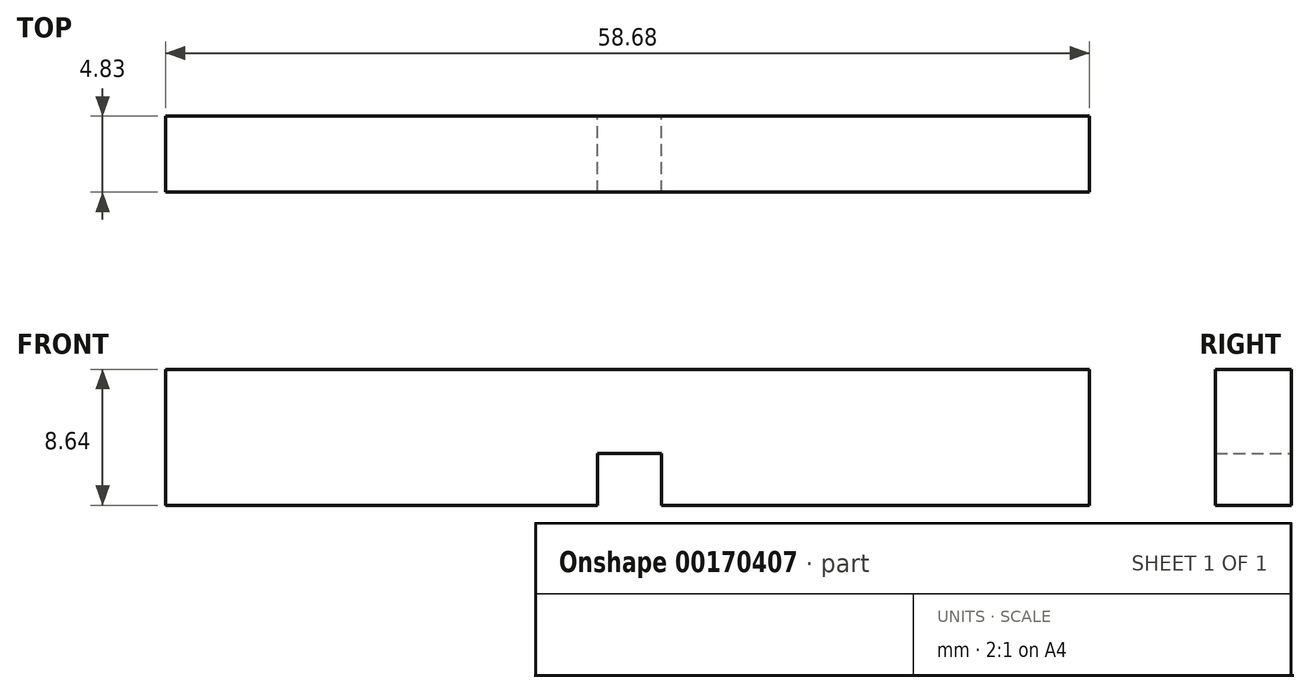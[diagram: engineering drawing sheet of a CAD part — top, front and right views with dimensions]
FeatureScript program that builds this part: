
annotation { "Feature Type Name" : "Feature", "Feature Type Description" : "" }
export const myFeature = defineFeature(function(context is Context, id is Id, definition is map)
    precondition{}
    {
        {
            var Q0;
            Q0=qCreatedBy(makeId("Front.planeOp"),FACE);
            var sketch = newSketch(context, id + "F0", { "sketchPlane" : qUnion([Q0])});
            skLineSegment(sketch, "E0.bottom", {"start": v(-29.34, 4.32) * mm, "end": v(29.34, 4.32) * mm});
            skLineSegment(sketch, "E0.top", {"start": v(-29.34, -4.32) * mm, "end": v(-1.9, -4.32) * mm});
            skLineSegment(sketch, "E0.left", {"start": v(-29.34, 4.32) * mm, "end": v(-29.34, -4.32) * mm});
            skLineSegment(sketch, "E0.right", {"start": v(29.34, 4.32) * mm, "end": v(29.34, -4.32) * mm});
            skLineSegment(sketch, "E1.bottom", {"start": v(-1.9, -1.02) * mm, "end": v(2.16, -1.02) * mm});
            skLineSegment(sketch, "E1.left", {"start": v(-1.9, -1.02) * mm, "end": v(-1.9, -4.32) * mm});
            skLineSegment(sketch, "E1.right", {"start": v(2.16, -1.02) * mm, "end": v(2.16, -4.32) * mm});
            skLineSegment(sketch, "E2.trimOffspring", {"start": v(2.16, -4.32) * mm, "end": v(29.34, -4.32) * mm});
            skPoint(sketch, "E1.top.end.orphan", {"position": v(2.16, -12.73) * mm});
            skPoint(sketch, "E1.top.start.orphan", {"position": v(-1.9, -12.73) * mm});
            skSolve(sketch);
        }
        {
            var Q0;
            Q0=makeQuery(id+"F0.imprint","IMPRINT",FACE,{"disambiguationData":[TD([[makeQuery(id+"F0.imprint","IMPRINT",EDGE,{"derivedFrom":sQuery(id+"F0.wireOp",EDGE,"E0.bottom")}),-1.0]])]});
            extrude(context, id + "F1", {"entities" : qUnion([Q0]), "depth" : 4.83 * mm});
        }
    });
